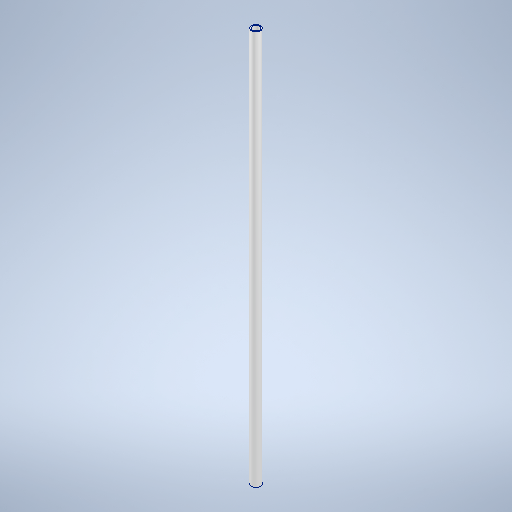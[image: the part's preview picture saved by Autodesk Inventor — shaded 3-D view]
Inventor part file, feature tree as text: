
AUTODESK INVENTOR PART (.ipt)
format: ipt  version: 2025 (Build 290162000, 162)  size: 253,952 bytes
history: native  units: mm
features: other x1, extrude x1, sketch x1
ambient origin geometry x8: Origin, YZ Plane, XZ Plane, XY Plane, X Axis, Y Axis, Z Axis, Center Point
bodies: Body1 (feature_tree)
feature tree (3):
  other  "Těleso1"
  extrude  "Vysunutí1"  Depth=8.0mm
  sketch  "Náčrt1"
